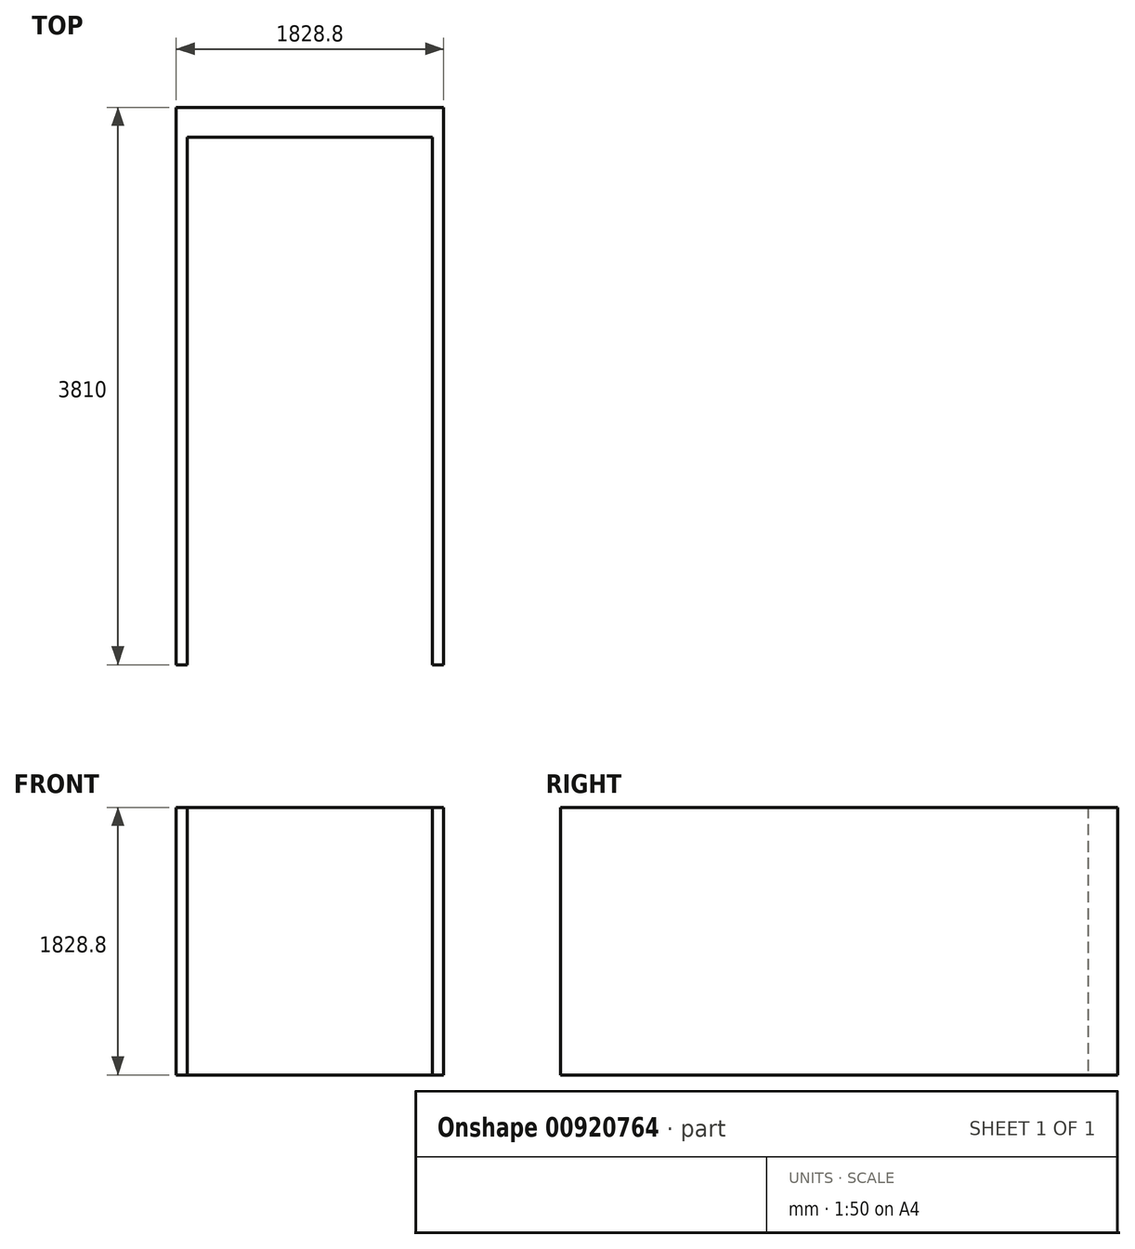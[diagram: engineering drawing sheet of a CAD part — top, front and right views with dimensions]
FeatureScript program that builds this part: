
annotation { "Feature Type Name" : "Feature", "Feature Type Description" : "" }
export const myFeature = defineFeature(function(context is Context, id is Id, definition is map)
    precondition{}
    {
        {
            var Q0;
            Q0=qCreatedBy(makeId("Top.planeOp"),FACE);
            var sketch = newSketch(context, id + "F0", { "sketchPlane" : qUnion([Q0])});
            skPoint(sketch, "E0.middle", {"position": v(0, 0) * mm});
            skLineSegment(sketch, "E1.bottom", {"start": v(914.4, 1905) * mm, "end": v(-914.4, 1905) * mm});
            skLineSegment(sketch, "E1.left", {"start": v(914.4, 1905) * mm, "end": v(914.4, -1905) * mm});
            skLineSegment(sketch, "E1.right", {"start": v(-914.4, 1905) * mm, "end": v(-914.4, -1905) * mm});
            skLineSegment(sketch, "E2", {"start": v(-914.4, -1905) * mm, "end": v(-838.2, -1905) * mm});
            skLineSegment(sketch, "E3", {"start": v(838.2, -1905) * mm, "end": v(914.4, -1905) * mm});
            skLineSegment(sketch, "E4", {"start": v(-838.2, -1905) * mm, "end": v(-838.2, 1701.8) * mm});
            skLineSegment(sketch, "E5", {"start": v(-838.2, 1701.8) * mm, "end": v(838.2, 1701.8) * mm});
            skLineSegment(sketch, "E6", {"start": v(838.2, 1701.8) * mm, "end": v(838.2, -1905) * mm});
            skSolve(sketch);
        }
        {
            var Q0;
            Q0 = qSketchRegion(id + "F0", true);
            extrude(context, id + "F1", {"entities" : qUnion([Q0]), "depth" : 1828.8 * mm, "offsetDistance" : 25.4 * mm});
        }
    });
